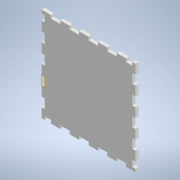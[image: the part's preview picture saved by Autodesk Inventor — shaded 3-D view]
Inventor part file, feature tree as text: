
AUTODESK INVENTOR PART (.ipt)
format: ipt  version: 2021 (Build 250183000, 183)  size: 195,072 bytes
history: native  units: mm
features: reference x20, other x6, plane x1, extrude x1, sketch x1
ambient origin geometry x8: Origin, YZ Plane, XZ Plane, XY Plane, X Axis, Y Axis, Z Axis, Center Point
bodies: Solid1 (feature_tree)
feature tree (29):
  plane  "Work Plane1"
  extrude  "Extrusion1"  Depth=120.0mm
  sketch  "Sketch1"  dims[d1=120.0mm d2=120.0mm d3=0.0mm d4=0.0mm d5=4.0mm d6=0.0mm]
  reference  "Reference1"
  reference  "Reference2"
  reference  "Reference3"
  reference  "Reference4"
  reference  "Reference5"
  reference  "Reference6"
  reference  "Reference7"
  reference  "Reference8"
  reference  "Reference9"
  reference  "Reference10"
  reference  "Reference11"
  reference  "Reference12"
  reference  "Reference13"
  reference  "Reference14"
  reference  "Reference15"
  reference  "Reference16"
  reference  "Reference17"
  reference  "Reference18"
  reference  "Reference19"
  reference  "Reference20"
  other  "<userpath>\Velaverkfraedi\Vor - 2023\Tolvustud_framleidsla\lukt_samsetning.iam"
  other  "lukt_samsetning.iam"
  other  "Lukt_hlidarplata:3"
  other  "Lukt_hlidarplata:1"
  other  "Lukt_hlidarplata:2"
  other  "Lukt_hlidarplata:4"
